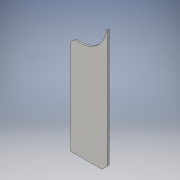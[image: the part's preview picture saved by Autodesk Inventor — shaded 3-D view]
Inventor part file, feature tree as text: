
AUTODESK INVENTOR PART (.ipt)
format: ipt  version: 2016 (Build 200138000, 138)  size: 109,568 bytes
history: native  units: in
note: dims shown in document units (in); Inventor stores cm internally (conversion verified against a paired STEP export)
features: hole x2, fillet x2, extrude x1, chamfer x1, sketch x1
ambient origin geometry x8: Origin, YZ Plane, XZ Plane, XY Plane, X Axis, Y Axis, Z Axis, Center Point
bodies: Solid1 (feature_tree)
feature tree (7):
  extrude  "Extrusion1"  Depth=12.0in
  chamfer  "Chamfer1"  Distance=0.15in
  hole  "Hole1"  [1 undecoded]
  hole  "Hole2"  [1 undecoded]
  fillet  "Fillet1"  Radius=0.3in
  fillet  "Fillet2"  Radius=0.5in
  sketch  "Sketch1"  dims[d0=3.25in d1=12.0in d2=0.15in d3=0.0in d4=0.5in d5=0.125in d6=45.0deg d7=0.8in d8=0.7in d9=5.0in d10=0.75in d11=0.375in d12=0.25in d13=0.5635in d14=1.0in d15=0.8108in d16=1.0in d17=1.0in d18=1.9in d19=0.75in d20=0.375in d21=0.25in d22=0.5635in d23=1.0in d24=0.8108in d25=0.3in d26=0.5in]
note: 2 required parameter values undecoded (feature->parameter linkage not recoverable at this tier; creation-order binding heuristic only, values carry confidence <= 0.55)
